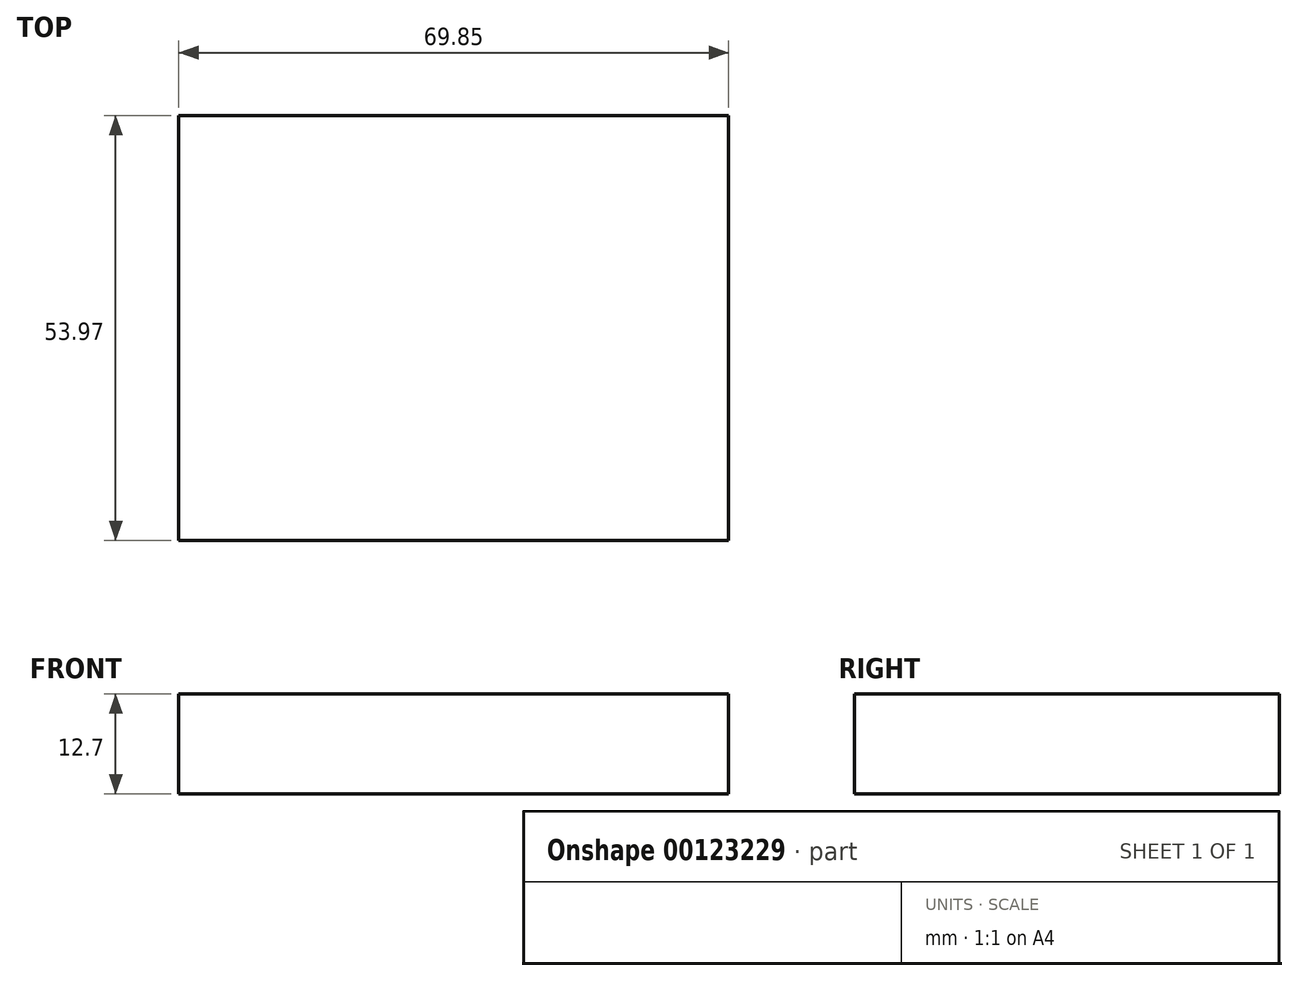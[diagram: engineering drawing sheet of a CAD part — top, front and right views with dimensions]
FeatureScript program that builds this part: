
annotation { "Feature Type Name" : "Feature", "Feature Type Description" : "" }
export const myFeature = defineFeature(function(context is Context, id is Id, definition is map)
    precondition{}
    {
        {
            var Q0;
            Q0=qCreatedBy(makeId("Top.planeOp"),FACE);
            var sketch = newSketch(context, id + "F0", { "sketchPlane" : qUnion([Q0])});
            skLineSegment(sketch, "E0.bottom", {"start": v(-33.04, 25.52) * mm, "end": v(36.8, 25.52) * mm});
            skLineSegment(sketch, "E0.top", {"start": v(-33.04, -28.45) * mm, "end": v(36.8, -28.45) * mm});
            skLineSegment(sketch, "E0.left", {"start": v(-33.04, 25.52) * mm, "end": v(-33.04, -28.45) * mm});
            skLineSegment(sketch, "E0.right", {"start": v(36.8, 25.52) * mm, "end": v(36.8, -28.45) * mm});
            skSolve(sketch);
        }
        {
            var Q0;
            Q0=makeQuery(id+"F0.imprint","IMPRINT",FACE,{"disambiguationData":[TD([[makeQuery(id+"F0.imprint","IMPRINT",EDGE,{"derivedFrom":sQuery(id+"F0.wireOp",EDGE,"E0.bottom")}),-1.0]])]});
            extrude(context, id + "F1", {"entities" : qUnion([Q0]), "depth" : 12.7 * mm});
        }
    });
